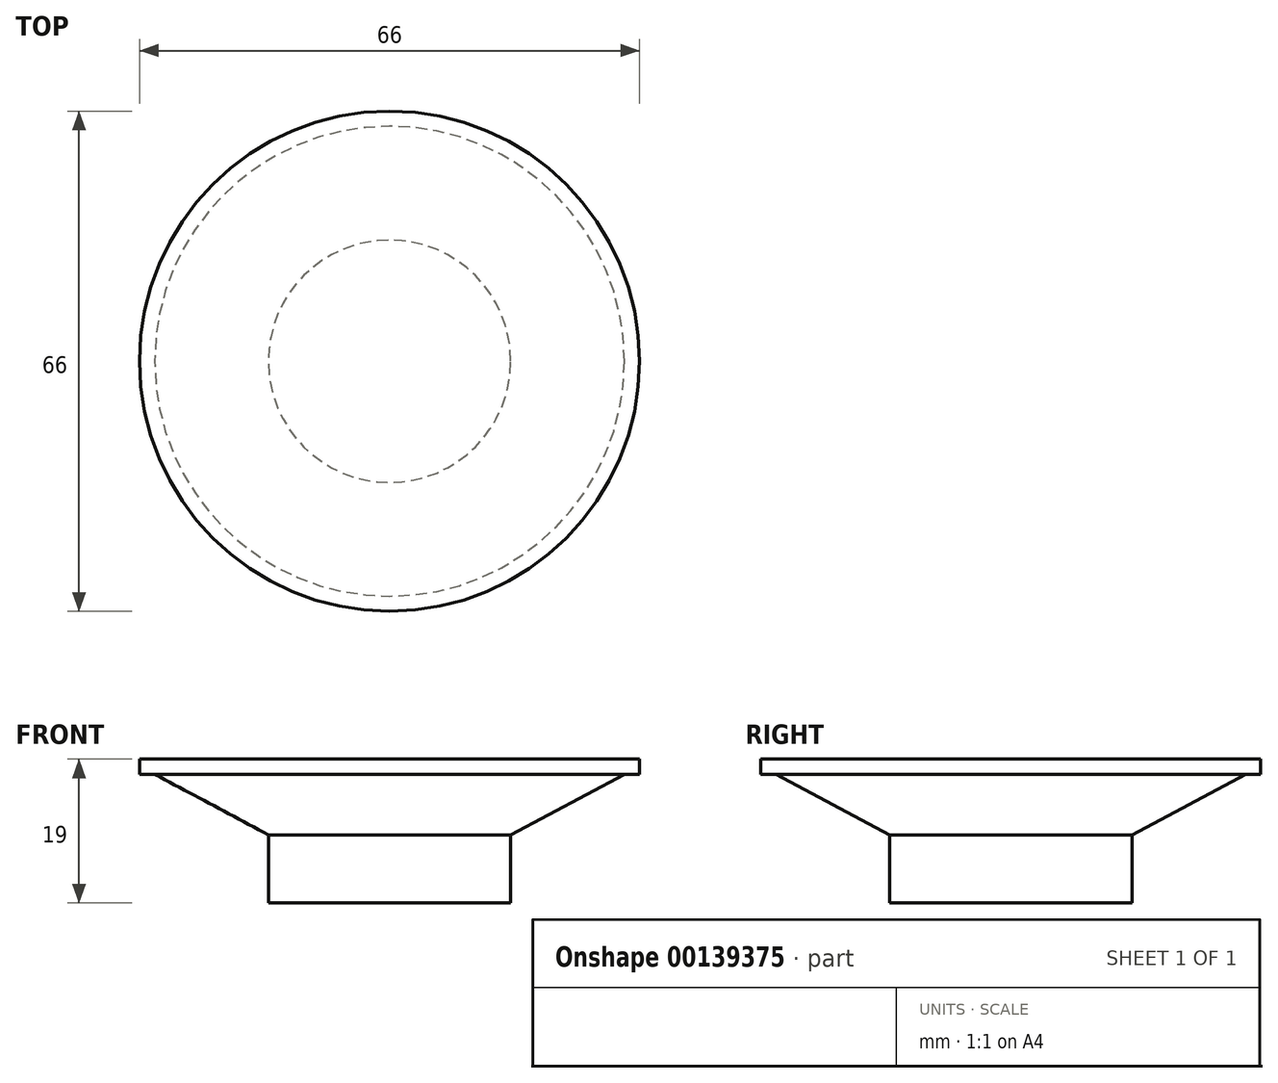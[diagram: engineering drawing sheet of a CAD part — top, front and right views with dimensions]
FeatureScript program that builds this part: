
annotation { "Feature Type Name" : "Feature", "Feature Type Description" : "" }
export const myFeature = defineFeature(function(context is Context, id is Id, definition is map)
    precondition{}
    {
        {
            var Q0;
            Q0=qCreatedBy(makeId("Front.planeOp"),FACE);
            var sketch = newSketch(context, id + "F0", { "sketchPlane" : qUnion([Q0])});
            skLineSegment(sketch, "E0", {"start": v(0, -8.64) * mm, "end": v(16, -8.64) * mm});
            skLineSegment(sketch, "E1", {"start": v(16, -8.64) * mm, "end": v(16, 0.36) * mm});
            skLineSegment(sketch, "E2", {"start": v(31, 8.36) * mm, "end": v(16, 0.36) * mm});
            skPoint(sketch, "E3.oppositeSnap0", {"position": v(15.5, 8.36) * mm});
            skLineSegment(sketch, "E3.bottom", {"start": v(0, 10.36) * mm, "end": v(33, 10.36) * mm});
            skLineSegment(sketch, "E3.top", {"start": v(31, 8.36) * mm, "end": v(33, 8.36) * mm});
            skLineSegment(sketch, "E3.right", {"start": v(33, 10.36) * mm, "end": v(33, 8.36) * mm});
            skPoint(sketch, "E4.start.orphan", {"position": v(0, 8.36) * mm});
            skLineSegment(sketch, "E5", {"start": v(0, -8.64) * mm, "end": v(0, 10.36) * mm});
            skSolve(sketch);
        }
        {
            var Q0;
            Q0 = qSketchRegion(id + "F0", true);
            var Q1;
            Q1=sQuery(id+"F0.wireOp",EDGE,"E5");
            revolve(context, id + "F1", {"entities" : qUnion([Q0]), "axis" : qUnion([Q1]), "revolveType" : RevolveType.FULL});
        }
    });
